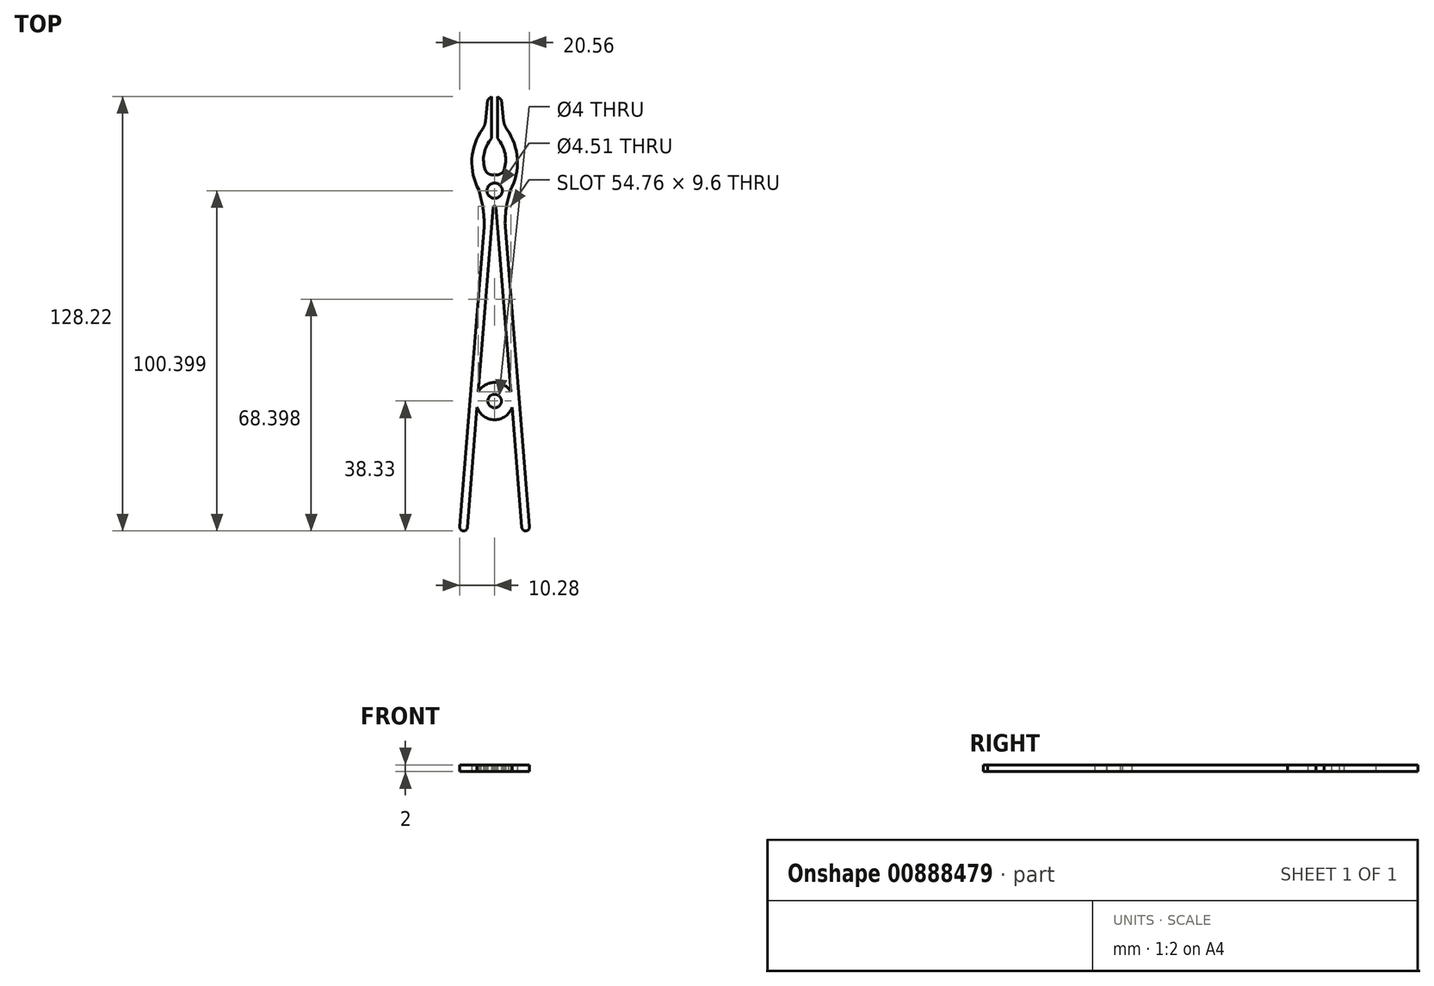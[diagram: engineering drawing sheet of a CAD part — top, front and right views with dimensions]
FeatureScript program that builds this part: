
annotation { "Feature Type Name" : "Feature", "Feature Type Description" : "" }
export const myFeature = defineFeature(function(context is Context, id is Id, definition is map)
    precondition{}
    {
        {
            var Q0;
            Q0=qCreatedBy(makeId("Top.planeOp"),FACE);
            var sketch = newSketch(context, id + "F0", { "sketchPlane" : qUnion([Q0])});
            skCircle(sketch, "E0", {"center": v(0, 0) * mm, "radius": 2 * mm});
            skLineSegment(sketch, "E1", {"start": v(-4.8, 2.69) * mm, "end": v(-0.37, 57.45) * mm});
            skLineSegment(sketch, "E2", {"start": v(5.17, -1.88) * mm, "end": v(8.03, -37.3) * mm});
            skPoint(sketch, "E3.trimOffspring.end.orphan", {"position": v(5.5, 0) * mm});
            skCircle(sketch, "E4", {"center": v(0, 62.07) * mm, "radius": 2.25 * mm});
            skArc(sketch, "E5", {"start": v(0.53, 66.67) * mm, "mid": v(0, 66.7) * mm, "end": v(-0.53, 66.67) * mm});
            skLineSegment(sketch, "E6", {"start": v(-3.1, 51.49) * mm, "end": v(-10.26, -37.04) * mm});
            skPoint(sketch, "E7.end.orphan", {"position": v(-0.9, -14.3) * mm});
            skArc(sketch, "E8", {"start": v(-5.17, -1.88) * mm, "mid": v(0, -5.5) * mm, "end": v(5.17, -1.88) * mm});
            skArc(sketch, "E9", {"start": v(2.73, 68.04) * mm, "mid": v(3.1, 73) * mm, "end": v(0.9, 77.47) * mm});
            skLineSegment(sketch, "E10", {"start": v(0.9, 77.47) * mm, "end": v(0.9, 89.9) * mm});
            skLineSegment(sketch, "E11", {"start": v(0.9, 89.9) * mm, "end": v(1.92, 88.98) * mm});
            skArc(sketch, "E12", {"start": v(4.63, 62.24) * mm, "mid": v(6.7, 71.4) * mm, "end": v(3.58, 80.25) * mm});
            skLineSegment(sketch, "E13", {"start": v(2.01, 88.8) * mm, "end": v(2.68, 82.62) * mm});
            skPoint(sketch, "E14.visualSharp", {"position": v(2.83, 81.23) * mm});
            skArc(sketch, "E14.filletArc", {"start": v(2.68, 82.62) * mm, "mid": v(2.98, 81.38) * mm, "end": v(3.58, 80.25) * mm});
            skPoint(sketch, "E15.visualSharp", {"position": v(2, 88.91) * mm});
            skArc(sketch, "E15.filletArc", {"start": v(2.01, 88.8) * mm, "mid": v(1.98, 88.9) * mm, "end": v(1.92, 88.98) * mm});
            skArc(sketch, "E16", {"start": v(0, 66.7) * mm, "mid": v(1.58, 66.94) * mm, "end": v(2.73, 68.04) * mm});
            skLineSegment(sketch, "E17.MirrorCS", {"start": v(-0.9, 77.47) * mm, "end": v(-0.9, 89.9) * mm});
            skArc(sketch, "E18.MirrorCS", {"start": v(-2.73, 68.04) * mm, "mid": v(-3.1, 73) * mm, "end": v(-0.9, 77.47) * mm});
            skArc(sketch, "E19.MirrorCS", {"start": v(0, 66.7) * mm, "mid": v(-1.58, 66.94) * mm, "end": v(-2.73, 68.04) * mm});
            skArc(sketch, "E20.MirrorCS", {"start": v(-4.63, 62.24) * mm, "mid": v(-6.7, 71.4) * mm, "end": v(-3.58, 80.25) * mm});
            skArc(sketch, "E21.MirrorCS", {"start": v(-2.68, 82.62) * mm, "mid": v(-2.98, 81.38) * mm, "end": v(-3.58, 80.25) * mm});
            skLineSegment(sketch, "E22.MirrorCS", {"start": v(-2.01, 88.8) * mm, "end": v(-2.68, 82.62) * mm});
            skLineSegment(sketch, "E23.MirrorCS", {"start": v(-0.9, 89.9) * mm, "end": v(-1.92, 88.98) * mm});
            skArc(sketch, "E24", {"start": v(4.08, 59.87) * mm, "mid": v(3.28, 55.71) * mm, "end": v(3.1, 51.49) * mm});
            skLineSegment(sketch, "E25", {"start": v(4.63, 62.24) * mm, "end": v(4.08, 59.87) * mm});
            skLineSegment(sketch, "E26.trimOffspring", {"start": v(3.1, 51.49) * mm, "end": v(10.26, -37.04) * mm});
            skPoint(sketch, "E27.start.orphan", {"position": v(2.25, 62.07) * mm});
            skLineSegment(sketch, "E28.trimOffspring", {"start": v(0.37, 57.45) * mm, "end": v(4.8, 2.69) * mm});
            skPoint(sketch, "E29.orphan", {"position": v(-2.25, 62.07) * mm});
            skArc(sketch, "E30.MirrorCS", {"start": v(-4.08, 59.87) * mm, "mid": v(-3.28, 55.71) * mm, "end": v(-3.1, 51.49) * mm});
            skLineSegment(sketch, "E31.MirrorCS", {"start": v(-4.63, 62.24) * mm, "end": v(-4.08, 59.87) * mm});
            skArc(sketch, "E32.trimOffspring", {"start": v(-0.37, 57.45) * mm, "mid": v(0, 57.43) * mm, "end": v(0.37, 57.45) * mm});
            skLineSegment(sketch, "E33", {"start": v(-3.1, 51.49) * mm, "end": v(-3.1, 51.49) * mm});
            skLineSegment(sketch, "E34.MirrorCS", {"start": v(-5.17, -1.88) * mm, "end": v(-8.03, -37.3) * mm});
            skArc(sketch, "E35.trimOffspring", {"start": v(4.8, 2.69) * mm, "mid": v(0, 5.5) * mm, "end": v(-4.8, 2.69) * mm});
            skPoint(sketch, "E36.orphan", {"position": v(5.02, 0) * mm});
            skPoint(sketch, "E37.orphan", {"position": v(-5.02, 0) * mm});
            skArc(sketch, "E38", {"start": v(8.03, -37.3) * mm, "mid": v(9.28, -38.32) * mm, "end": v(10.26, -37.04) * mm});
            skArc(sketch, "E39.MirrorCS", {"start": v(-8.03, -37.3) * mm, "mid": v(-9.28, -38.32) * mm, "end": v(-10.26, -37.04) * mm});
            skArc(sketch, "E40.MirrorCS", {"start": v(-2.01, 88.8) * mm, "mid": v(-1.98, 88.9) * mm, "end": v(-1.92, 88.98) * mm});
            skSolve(sketch);
        }
        {
            var Q0;
            Q0=makeQuery(id+"F0.imprint","IMPRINT",FACE,{"disambiguationData":[TD([[makeQuery(id+"F0.imprint","IMPRINT",EDGE,{"derivedFrom":sQuery(id+"F0.wireOp",EDGE,"E0")}),-1.0]])]});
            extrude(context, id + "F1", {"entities" : qUnion([Q0]), "depth" : 2 * mm, "offsetDistance" : 25 * mm});
        }
    });
